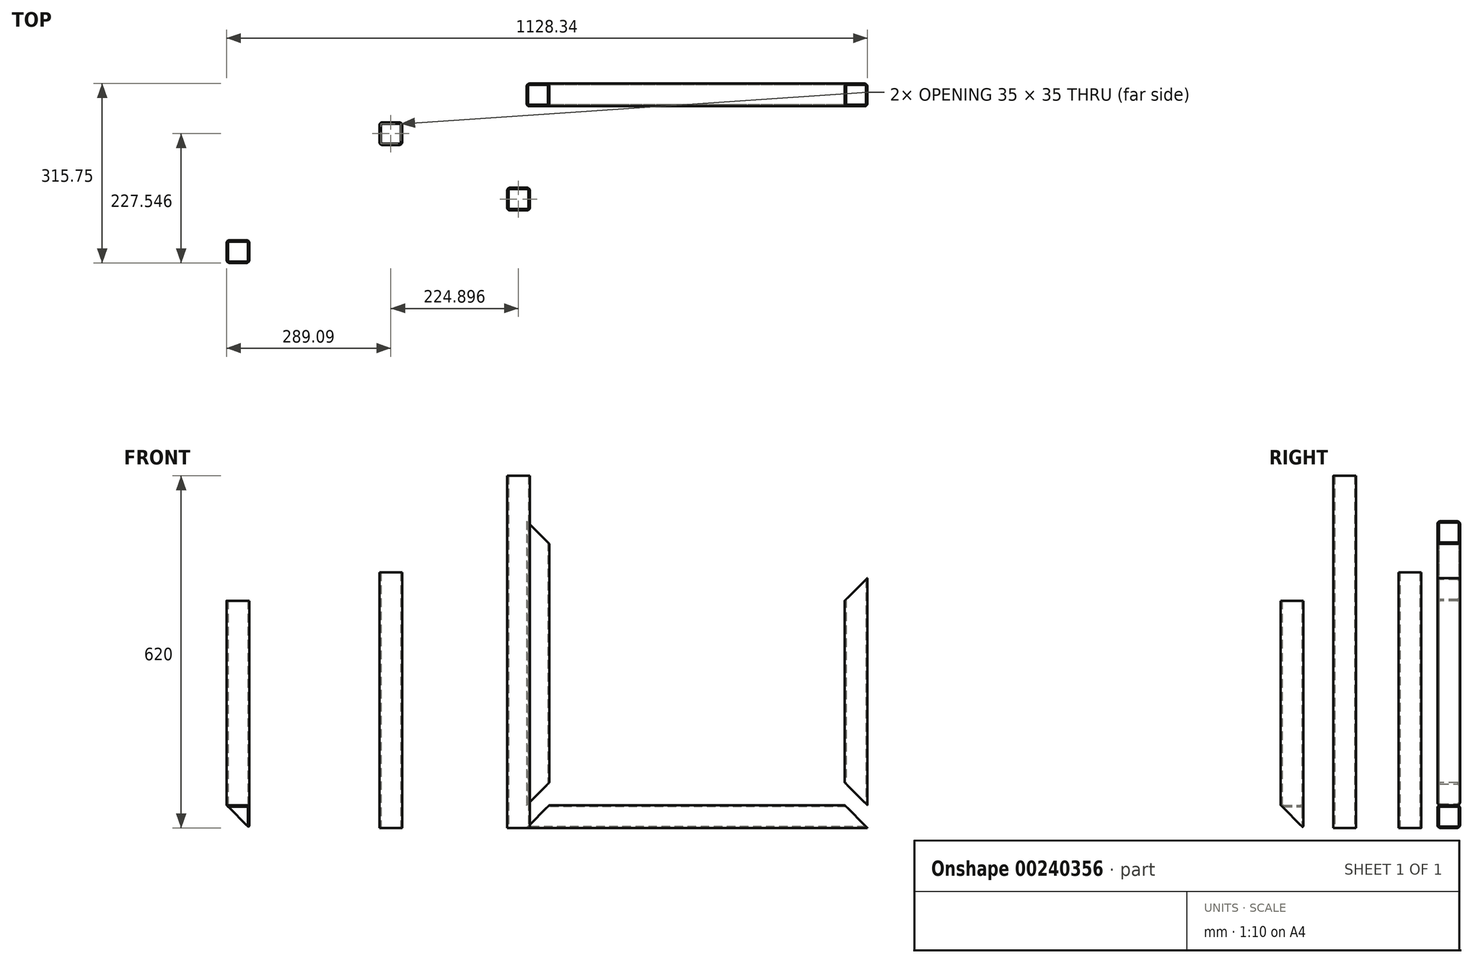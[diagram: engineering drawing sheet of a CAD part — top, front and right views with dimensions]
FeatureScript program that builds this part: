
annotation { "Feature Type Name" : "Feature", "Feature Type Description" : "" }
export const myFeature = defineFeature(function(context is Context, id is Id, definition is map)
    precondition{}
    {
        {
            var Q0;
            Q0=qCreatedBy(makeId("Right.planeOp"),FACE);
            var sketch = newSketch(context, id + "F0", { "sketchPlane" : qUnion([Q0])});
            skLineSegment(sketch, "E0.bottom", {"start": v(5, 0) * mm, "end": v(35, 0) * mm});
            skLineSegment(sketch, "E0.top", {"start": v(5, 40) * mm, "end": v(35, 40) * mm});
            skLineSegment(sketch, "E0.left", {"start": v(0, 5) * mm, "end": v(0, 35) * mm});
            skLineSegment(sketch, "E0.right", {"start": v(40, 5) * mm, "end": v(40, 35) * mm});
            skPoint(sketch, "E1.visualSharp", {"position": v(0, 40) * mm});
            skArc(sketch, "E1.filletArc", {"start": v(5, 40) * mm, "mid": v(1.46, 38.54) * mm, "end": v(0, 35) * mm});
            skPoint(sketch, "E2.visualSharp", {"position": v(40, 40) * mm});
            skArc(sketch, "E2.filletArc", {"start": v(40, 35) * mm, "mid": v(38.54, 38.54) * mm, "end": v(35, 40) * mm});
            skPoint(sketch, "E3.visualSharp", {"position": v(40, 0) * mm});
            skArc(sketch, "E3.filletArc", {"start": v(35, 0) * mm, "mid": v(38.54, 1.46) * mm, "end": v(40, 5) * mm});
            skPoint(sketch, "E4.visualSharp", {"position": v(0, 0) * mm});
            skArc(sketch, "E4.filletArc", {"start": v(0, 5) * mm, "mid": v(1.46, 1.46) * mm, "end": v(5, 0) * mm});
            skArc(sketch, "E5.0", {"start": v(35, 2.5) * mm, "mid": v(36.77, 3.23) * mm, "end": v(37.5, 5) * mm});
            skLineSegment(sketch, "E5.1", {"start": v(5, 2.5) * mm, "end": v(35, 2.5) * mm});
            skLineSegment(sketch, "E5.2", {"start": v(37.5, 5) * mm, "end": v(37.5, 35) * mm});
            skArc(sketch, "E5.3", {"start": v(2.5, 5) * mm, "mid": v(3.23, 3.23) * mm, "end": v(5, 2.5) * mm});
            skArc(sketch, "E5.4", {"start": v(37.5, 35) * mm, "mid": v(36.77, 36.77) * mm, "end": v(35, 37.5) * mm});
            skLineSegment(sketch, "E5.5", {"start": v(5, 37.5) * mm, "end": v(35, 37.5) * mm});
            skArc(sketch, "E5.6", {"start": v(5, 37.5) * mm, "mid": v(3.23, 36.77) * mm, "end": v(2.5, 35) * mm});
            skLineSegment(sketch, "E5.7", {"start": v(2.5, 5) * mm, "end": v(2.5, 35) * mm});
            skSolve(sketch);
        }
        {
            var Q0;
            Q0=makeQuery(id+"F0.imprint","IMPRINT",FACE,{"disambiguationData":[TD([[makeQuery(id+"F0.imprint","IMPRINT",EDGE,{"derivedFrom":sQuery(id+"F0.wireOp",EDGE,"E0.bottom")}),1.0]])]});
            extrude(context, id + "F1", {"entities" : qUnion([Q0]), "depth" : 600 * mm});
        }
        {
            var Q0;
            Q0=makeQuery(id+"F1.opExtrude","SWEPT_FACE",FACE,{"disambiguationData":[OSD([sQuery(id+"F0.wireOp",EDGE,"E0.left")])]});
            var sketch = newSketch(context, id + "F2", { "sketchPlane" : qUnion([Q0])});
            skLineSegment(sketch, "E6", {"start": v(0, 0) * mm, "end": v(0, 40) * mm});
            skLineSegment(sketch, "E7", {"start": v(0, 40) * mm, "end": v(40, 40) * mm});
            skLineSegment(sketch, "E8", {"start": v(40, 40) * mm, "end": v(0, 0) * mm});
            skLineSegment(sketch, "E9", {"start": v(600, 0) * mm, "end": v(600, 40) * mm});
            skLineSegment(sketch, "E10", {"start": v(600, 40) * mm, "end": v(560, 40) * mm});
            skLineSegment(sketch, "E11", {"start": v(560, 40) * mm, "end": v(600, 0) * mm});
            skSolve(sketch);
        }
        {
            var Q0;
            Q0 = qSketchRegion(id + "F2", true);
            extrude(context, id + "F3", {"entities" : qUnion([Q0]), "operationType" : NewBodyOperationType.REMOVE, "endBound" : BoundingType.THROUGH_ALL, "oppositeDirection" : true, "depth" : 25 * mm});
        }
        {
            var Q0;
            Q0=makeQuery(id+"F1.opExtrude","SWEPT_FACE",FACE,{"disambiguationData":[OSD([sQuery(id+"F0.wireOp",EDGE,"E0.top")])]});
            var sketch = newSketch(context, id + "F4", { "sketchPlane" : qUnion([Q0])});
            skLineSegment(sketch, "E12.bottom", {"start": v(5, 0) * mm, "end": v(35, 0) * mm});
            skLineSegment(sketch, "E12.top", {"start": v(5, 40) * mm, "end": v(35, 40) * mm});
            skLineSegment(sketch, "E12.left", {"start": v(0, 5) * mm, "end": v(0, 35) * mm});
            skLineSegment(sketch, "E12.right", {"start": v(40, 5) * mm, "end": v(40, 35) * mm});
            skPoint(sketch, "E13.visualSharp", {"position": v(0, 40) * mm});
            skArc(sketch, "E13.filletArc", {"start": v(5, 40) * mm, "mid": v(1.46, 38.54) * mm, "end": v(0, 35) * mm});
            skPoint(sketch, "E14.visualSharp", {"position": v(40, 40) * mm});
            skArc(sketch, "E14.filletArc", {"start": v(40, 35) * mm, "mid": v(38.54, 38.54) * mm, "end": v(35, 40) * mm});
            skPoint(sketch, "E15.visualSharp", {"position": v(40, 0) * mm});
            skArc(sketch, "E15.filletArc", {"start": v(35, 0) * mm, "mid": v(38.54, 1.46) * mm, "end": v(40, 5) * mm});
            skPoint(sketch, "E16.visualSharp", {"position": v(0, 0) * mm});
            skArc(sketch, "E16.filletArc", {"start": v(0, 5) * mm, "mid": v(1.46, 1.46) * mm, "end": v(5, 0) * mm});
            skArc(sketch, "E17.0", {"start": v(35, 2.5) * mm, "mid": v(36.77, 3.23) * mm, "end": v(37.5, 5) * mm});
            skLineSegment(sketch, "E17.1", {"start": v(5, 2.5) * mm, "end": v(35, 2.5) * mm});
            skLineSegment(sketch, "E17.2", {"start": v(37.5, 5) * mm, "end": v(37.5, 35) * mm});
            skArc(sketch, "E17.3", {"start": v(2.5, 5) * mm, "mid": v(3.23, 3.23) * mm, "end": v(5, 2.5) * mm});
            skArc(sketch, "E17.4", {"start": v(37.5, 35) * mm, "mid": v(36.77, 36.77) * mm, "end": v(35, 37.5) * mm});
            skLineSegment(sketch, "E17.5", {"start": v(5, 37.5) * mm, "end": v(35, 37.5) * mm});
            skArc(sketch, "E17.6", {"start": v(5, 37.5) * mm, "mid": v(3.23, 36.77) * mm, "end": v(2.5, 35) * mm});
            skLineSegment(sketch, "E17.7", {"start": v(2.5, 5) * mm, "end": v(2.5, 35) * mm});
            skSolve(sketch);
        }
        {
            var Q0;
            Q0=makeQuery(id+"F4.imprint","IMPRINT",FACE,{"disambiguationData":[TD([[makeQuery(id+"F4.imprint","IMPRINT",EDGE,{"derivedFrom":sQuery(id+"F4.wireOp",EDGE,"E12.bottom")}),1.0]])]});
            extrude(context, id + "F5", {"entities" : qUnion([Q0]), "depth" : 500 * mm});
        }
        {
            var Q0;
            Q0=makeQuery(id+"F5.opExtrude","SWEPT_FACE",FACE,{"disambiguationData":[OSD([sQuery(id+"F4.wireOp",EDGE,"E12.bottom")])]});
            var sketch = newSketch(context, id + "F6", { "sketchPlane" : qUnion([Q0])});
            skLineSegment(sketch, "E18", {"start": v(0, 40) * mm, "end": v(40, 40) * mm});
            skLineSegment(sketch, "E19", {"start": v(40, 40) * mm, "end": v(40, 80) * mm});
            skLineSegment(sketch, "E20", {"start": v(40, 80) * mm, "end": v(0, 40) * mm});
            skLineSegment(sketch, "E21", {"start": v(40, 540) * mm, "end": v(40, 500) * mm});
            skLineSegment(sketch, "E22", {"start": v(40, 500) * mm, "end": v(0, 540) * mm});
            skLineSegment(sketch, "E23", {"start": v(0, 540) * mm, "end": v(40, 540) * mm});
            skSolve(sketch);
        }
        {
            var Q0;
            Q0 = qSketchRegion(id + "F6", true);
            extrude(context, id + "F7", {"entities" : qUnion([Q0]), "operationType" : NewBodyOperationType.REMOVE, "endBound" : BoundingType.THROUGH_ALL, "oppositeDirection" : true, "depth" : 25 * mm});
        }
        {
            var Q0;
            Q0=makeQuery(id+"F1.opExtrude","SWEPT_FACE",FACE,{"disambiguationData":[OSD([sQuery(id+"F0.wireOp",EDGE,"E0.top")])]});
            var sketch = newSketch(context, id + "F8", { "sketchPlane" : qUnion([Q0])});
            skLineSegment(sketch, "E24.bottom", {"start": v(565, 0) * mm, "end": v(595, 0) * mm});
            skLineSegment(sketch, "E24.top", {"start": v(565, 40) * mm, "end": v(595, 40) * mm});
            skLineSegment(sketch, "E24.left", {"start": v(560, 5) * mm, "end": v(560, 35) * mm});
            skLineSegment(sketch, "E24.right", {"start": v(600, 5) * mm, "end": v(600, 35) * mm});
            skPoint(sketch, "E25.visualSharp", {"position": v(560, 40) * mm});
            skArc(sketch, "E25.filletArc", {"start": v(565, 40) * mm, "mid": v(561.46, 38.54) * mm, "end": v(560, 35) * mm});
            skPoint(sketch, "E26.visualSharp", {"position": v(600, 40) * mm});
            skArc(sketch, "E26.filletArc", {"start": v(600, 35) * mm, "mid": v(598.54, 38.54) * mm, "end": v(595, 40) * mm});
            skPoint(sketch, "E27.visualSharp", {"position": v(600, 0) * mm});
            skArc(sketch, "E27.filletArc", {"start": v(595, 0) * mm, "mid": v(598.54, 1.46) * mm, "end": v(600, 5) * mm});
            skPoint(sketch, "E28.visualSharp", {"position": v(560, 0) * mm});
            skArc(sketch, "E28.filletArc", {"start": v(560, 5) * mm, "mid": v(561.46, 1.46) * mm, "end": v(565, 0) * mm});
            skArc(sketch, "E29.0", {"start": v(595, 2.5) * mm, "mid": v(596.77, 3.23) * mm, "end": v(597.5, 5) * mm});
            skLineSegment(sketch, "E29.1", {"start": v(565, 2.5) * mm, "end": v(595, 2.5) * mm});
            skLineSegment(sketch, "E29.2", {"start": v(597.5, 5) * mm, "end": v(597.5, 35) * mm});
            skArc(sketch, "E29.3", {"start": v(562.5, 5) * mm, "mid": v(563.23, 3.23) * mm, "end": v(565, 2.5) * mm});
            skArc(sketch, "E29.4", {"start": v(597.5, 35) * mm, "mid": v(596.77, 36.77) * mm, "end": v(595, 37.5) * mm});
            skLineSegment(sketch, "E29.5", {"start": v(565, 37.5) * mm, "end": v(595, 37.5) * mm});
            skArc(sketch, "E29.6", {"start": v(565, 37.5) * mm, "mid": v(563.23, 36.77) * mm, "end": v(562.5, 35) * mm});
            skLineSegment(sketch, "E29.7", {"start": v(562.5, 5) * mm, "end": v(562.5, 35) * mm});
            skSolve(sketch);
        }
        {
            var Q0;
            Q0 = qSketchRegion(id + "F8", true);
            extrude(context, id + "F9", {"entities" : qUnion([Q0]), "depth" : 400 * mm});
        }
        {
            var Q0;
            Q0=makeQuery(id+"F9.opExtrude","SWEPT_FACE",FACE,{"disambiguationData":[OSD([sQuery(id+"F8.wireOp",EDGE,"E24.bottom")])]});
            var sketch = newSketch(context, id + "F10", { "sketchPlane" : qUnion([Q0])});
            skLineSegment(sketch, "E30", {"start": v(600, 440) * mm, "end": v(560, 440) * mm});
            skLineSegment(sketch, "E31", {"start": v(560, 440) * mm, "end": v(560, 400) * mm});
            skLineSegment(sketch, "E32", {"start": v(560, 400) * mm, "end": v(600, 440) * mm});
            skLineSegment(sketch, "E33", {"start": v(560, 80) * mm, "end": v(560, 40) * mm});
            skLineSegment(sketch, "E34", {"start": v(560, 40) * mm, "end": v(600, 40) * mm});
            skLineSegment(sketch, "E35", {"start": v(600, 40) * mm, "end": v(560, 80) * mm});
            skSolve(sketch);
        }
        {
            var Q0;
            Q0 = qSketchRegion(id + "F10", true);
            extrude(context, id + "F11", {"entities" : qUnion([Q0]), "operationType" : NewBodyOperationType.REMOVE, "endBound" : BoundingType.THROUGH_ALL, "oppositeDirection" : true, "depth" : 25 * mm});
        }
        {
            var Q0;
            Q0=qCreatedBy(makeId("Top.planeOp"),FACE);
            var sketch = newSketch(context, id + "F12", { "sketchPlane" : qUnion([Q0])});
            skLineSegment(sketch, "E36.bottom", {"start": v(-29.35, -183.38) * mm, "end": v(0.65, -183.38) * mm});
            skLineSegment(sketch, "E36.top", {"start": v(-29.35, -143.38) * mm, "end": v(0.65, -143.38) * mm});
            skLineSegment(sketch, "E36.left", {"start": v(-34.35, -178.38) * mm, "end": v(-34.35, -148.38) * mm});
            skLineSegment(sketch, "E36.right", {"start": v(5.65, -178.38) * mm, "end": v(5.65, -148.38) * mm});
            skPoint(sketch, "E37.visualSharp", {"position": v(-34.35, -143.38) * mm});
            skArc(sketch, "E37.filletArc", {"start": v(-29.35, -143.38) * mm, "mid": v(-32.89, -144.84) * mm, "end": v(-34.35, -148.38) * mm});
            skPoint(sketch, "E38.visualSharp", {"position": v(5.65, -143.38) * mm});
            skArc(sketch, "E38.filletArc", {"start": v(5.65, -148.38) * mm, "mid": v(4.18, -144.84) * mm, "end": v(0.65, -143.38) * mm});
            skPoint(sketch, "E39.visualSharp", {"position": v(5.65, -183.38) * mm});
            skArc(sketch, "E39.filletArc", {"start": v(0.65, -183.38) * mm, "mid": v(4.18, -181.91) * mm, "end": v(5.65, -178.38) * mm});
            skPoint(sketch, "E40.visualSharp", {"position": v(-34.35, -183.38) * mm});
            skArc(sketch, "E40.filletArc", {"start": v(-34.35, -178.38) * mm, "mid": v(-32.89, -181.91) * mm, "end": v(-29.35, -183.38) * mm});
            skArc(sketch, "E41.0", {"start": v(0.65, -180.88) * mm, "mid": v(2.41, -180.15) * mm, "end": v(3.15, -178.38) * mm});
            skLineSegment(sketch, "E41.1", {"start": v(-29.35, -180.88) * mm, "end": v(0.65, -180.88) * mm});
            skLineSegment(sketch, "E41.2", {"start": v(3.15, -178.38) * mm, "end": v(3.15, -148.38) * mm});
            skArc(sketch, "E41.3", {"start": v(-31.85, -178.38) * mm, "mid": v(-31.12, -180.15) * mm, "end": v(-29.35, -180.88) * mm});
            skArc(sketch, "E41.4", {"start": v(3.15, -148.38) * mm, "mid": v(2.41, -146.61) * mm, "end": v(0.65, -145.88) * mm});
            skLineSegment(sketch, "E41.5", {"start": v(-29.35, -145.88) * mm, "end": v(0.65, -145.88) * mm});
            skArc(sketch, "E41.6", {"start": v(-29.35, -145.88) * mm, "mid": v(-31.12, -146.61) * mm, "end": v(-31.85, -148.38) * mm});
            skLineSegment(sketch, "E41.7", {"start": v(-31.85, -178.38) * mm, "end": v(-31.85, -148.38) * mm});
            skSolve(sketch);
        }
        {
            var Q0;
            Q0=makeQuery(id+"F12.imprint","IMPRINT",FACE,{"disambiguationData":[TD([[makeQuery(id+"F12.imprint","IMPRINT",EDGE,{"derivedFrom":sQuery(id+"F12.wireOp",EDGE,"E36.bottom")}),1.0]])]});
            extrude(context, id + "F13", {"entities" : qUnion([Q0]), "depth" : 620 * mm});
        }
        {
            var Q0;
            Q0=qCreatedBy(makeId("Top.planeOp"),FACE);
            var sketch = newSketch(context, id + "F14", { "sketchPlane" : qUnion([Q0])});
            skLineSegment(sketch, "E42.bottom", {"start": v(-254.25, -68.2) * mm, "end": v(-224.25, -68.2) * mm});
            skLineSegment(sketch, "E42.top", {"start": v(-254.25, -28.2) * mm, "end": v(-224.25, -28.2) * mm});
            skLineSegment(sketch, "E42.left", {"start": v(-259.25, -63.2) * mm, "end": v(-259.25, -33.2) * mm});
            skLineSegment(sketch, "E42.right", {"start": v(-219.25, -63.2) * mm, "end": v(-219.25, -33.2) * mm});
            skPoint(sketch, "E43.visualSharp", {"position": v(-259.25, -28.2) * mm});
            skArc(sketch, "E43.filletArc", {"start": v(-254.25, -28.2) * mm, "mid": v(-257.79, -29.67) * mm, "end": v(-259.25, -33.2) * mm});
            skPoint(sketch, "E44.visualSharp", {"position": v(-219.25, -28.2) * mm});
            skArc(sketch, "E44.filletArc", {"start": v(-219.25, -33.2) * mm, "mid": v(-220.71, -29.67) * mm, "end": v(-224.25, -28.2) * mm});
            skPoint(sketch, "E45.visualSharp", {"position": v(-219.25, -68.2) * mm});
            skArc(sketch, "E45.filletArc", {"start": v(-224.25, -68.2) * mm, "mid": v(-220.71, -66.74) * mm, "end": v(-219.25, -63.2) * mm});
            skPoint(sketch, "E46.visualSharp", {"position": v(-259.25, -68.2) * mm});
            skArc(sketch, "E46.filletArc", {"start": v(-259.25, -63.2) * mm, "mid": v(-257.79, -66.74) * mm, "end": v(-254.25, -68.2) * mm});
            skArc(sketch, "E47.0", {"start": v(-224.25, -65.7) * mm, "mid": v(-222.48, -64.97) * mm, "end": v(-221.75, -63.2) * mm});
            skLineSegment(sketch, "E47.1", {"start": v(-254.25, -65.7) * mm, "end": v(-224.25, -65.7) * mm});
            skLineSegment(sketch, "E47.2", {"start": v(-221.75, -63.2) * mm, "end": v(-221.75, -33.2) * mm});
            skArc(sketch, "E47.3", {"start": v(-256.75, -63.2) * mm, "mid": v(-256.02, -64.97) * mm, "end": v(-254.25, -65.7) * mm});
            skArc(sketch, "E47.4", {"start": v(-221.75, -33.2) * mm, "mid": v(-222.48, -31.44) * mm, "end": v(-224.25, -30.7) * mm});
            skLineSegment(sketch, "E47.5", {"start": v(-254.25, -30.7) * mm, "end": v(-224.25, -30.7) * mm});
            skArc(sketch, "E47.6", {"start": v(-254.25, -30.7) * mm, "mid": v(-256.02, -31.44) * mm, "end": v(-256.75, -33.2) * mm});
            skLineSegment(sketch, "E47.7", {"start": v(-256.75, -63.2) * mm, "end": v(-256.75, -33.2) * mm});
            skSolve(sketch);
        }
        {
            var Q0;
            Q0=makeQuery(id+"F14.imprint","IMPRINT",FACE,{"disambiguationData":[TD([[makeQuery(id+"F14.imprint","IMPRINT",EDGE,{"derivedFrom":sQuery(id+"F14.wireOp",EDGE,"E42.bottom")}),1.0]])]});
            extrude(context, id + "F15", {"entities" : qUnion([Q0]), "depth" : 450 * mm});
        }
        {
            var Q0;
            Q0=qCreatedBy(makeId("Top.planeOp"),FACE);
            var sketch = newSketch(context, id + "F16", { "sketchPlane" : qUnion([Q0])});
            skLineSegment(sketch, "E48.bottom", {"start": v(-523.34, -275.75) * mm, "end": v(-493.34, -275.75) * mm});
            skLineSegment(sketch, "E48.top", {"start": v(-523.34, -235.75) * mm, "end": v(-493.34, -235.75) * mm});
            skLineSegment(sketch, "E48.left", {"start": v(-528.34, -270.75) * mm, "end": v(-528.34, -240.75) * mm});
            skLineSegment(sketch, "E48.right", {"start": v(-488.34, -270.75) * mm, "end": v(-488.34, -240.75) * mm});
            skPoint(sketch, "E49.visualSharp", {"position": v(-528.34, -235.75) * mm});
            skArc(sketch, "E49.filletArc", {"start": v(-523.34, -235.75) * mm, "mid": v(-526.87, -237.21) * mm, "end": v(-528.34, -240.75) * mm});
            skPoint(sketch, "E50.visualSharp", {"position": v(-488.34, -235.75) * mm});
            skArc(sketch, "E50.filletArc", {"start": v(-488.34, -240.75) * mm, "mid": v(-489.8, -237.21) * mm, "end": v(-493.34, -235.75) * mm});
            skPoint(sketch, "E51.visualSharp", {"position": v(-488.34, -275.75) * mm});
            skArc(sketch, "E51.filletArc", {"start": v(-493.34, -275.75) * mm, "mid": v(-489.8, -274.29) * mm, "end": v(-488.34, -270.75) * mm});
            skPoint(sketch, "E52.visualSharp", {"position": v(-528.34, -275.75) * mm});
            skArc(sketch, "E52.filletArc", {"start": v(-528.34, -270.75) * mm, "mid": v(-526.87, -274.29) * mm, "end": v(-523.34, -275.75) * mm});
            skArc(sketch, "E53.0", {"start": v(-493.34, -273.25) * mm, "mid": v(-491.57, -272.52) * mm, "end": v(-490.84, -270.75) * mm});
            skLineSegment(sketch, "E53.1", {"start": v(-523.34, -273.25) * mm, "end": v(-493.34, -273.25) * mm});
            skLineSegment(sketch, "E53.2", {"start": v(-490.84, -270.75) * mm, "end": v(-490.84, -240.75) * mm});
            skArc(sketch, "E53.3", {"start": v(-525.84, -270.75) * mm, "mid": v(-525.1, -272.52) * mm, "end": v(-523.34, -273.25) * mm});
            skArc(sketch, "E53.4", {"start": v(-490.84, -240.75) * mm, "mid": v(-491.57, -238.98) * mm, "end": v(-493.34, -238.25) * mm});
            skLineSegment(sketch, "E53.5", {"start": v(-523.34, -238.25) * mm, "end": v(-493.34, -238.25) * mm});
            skArc(sketch, "E53.6", {"start": v(-523.34, -238.25) * mm, "mid": v(-525.1, -238.98) * mm, "end": v(-525.84, -240.75) * mm});
            skLineSegment(sketch, "E53.7", {"start": v(-525.84, -270.75) * mm, "end": v(-525.84, -240.75) * mm});
            skSolve(sketch);
        }
        {
            var Q0;
            Q0=makeQuery(id+"F16.imprint","IMPRINT",FACE,{"disambiguationData":[TD([[makeQuery(id+"F16.imprint","IMPRINT",EDGE,{"derivedFrom":sQuery(id+"F16.wireOp",EDGE,"E48.bottom")}),1.0]])]});
            extrude(context, id + "F17", {"entities" : qUnion([Q0]), "depth" : 400 * mm});
        }
        {
            var Q0;
            Q0=makeQuery(id+"F17.opExtrude","SWEPT_FACE",FACE,{"disambiguationData":[OSD([sQuery(id+"F16.wireOp",EDGE,"E48.right")])]});
            var sketch = newSketch(context, id + "F18", { "sketchPlane" : qUnion([Q0])});
            skLineSegment(sketch, "E54", {"start": v(-235.75, 0) * mm, "end": v(-275.75, 40) * mm});
            skLineSegment(sketch, "E55", {"start": v(-235.75, 0) * mm, "end": v(-275.75, 0) * mm});
            skLineSegment(sketch, "E56", {"start": v(-275.75, 0) * mm, "end": v(-275.75, 40) * mm});
            skSolve(sketch);
        }
        {
            var Q0;
            Q0=makeQuery(id+"F17.opExtrude","SWEPT_FACE",FACE,{"disambiguationData":[OSD([sQuery(id+"F16.wireOp",EDGE,"E48.top")])]});
            var sketch = newSketch(context, id + "F19", { "sketchPlane" : qUnion([Q0])});
            skLineSegment(sketch, "E57.MirrorCS", {"start": v(528.34, 40) * mm, "end": v(488.34, 0) * mm});
            skLineSegment(sketch, "E58", {"start": v(488.34, 0) * mm, "end": v(528.34, 0) * mm});
            skLineSegment(sketch, "E59", {"start": v(528.34, 0) * mm, "end": v(528.34, 40) * mm});
            skSolve(sketch);
        }
        {
            var Q0;
            Q0 = qSketchRegion(id + "F18", true);
            extrude(context, id + "F20", {"entities" : qUnion([Q0]), "operationType" : NewBodyOperationType.REMOVE, "endBound" : BoundingType.THROUGH_ALL, "oppositeDirection" : true, "depth" : 25 * mm});
        }
        {
            var Q0;
            Q0 = qSketchRegion(id + "F19", true);
            extrude(context, id + "F21", {"entities" : qUnion([Q0]), "operationType" : NewBodyOperationType.REMOVE, "endBound" : BoundingType.THROUGH_ALL, "oppositeDirection" : true, "depth" : 25 * mm});
        }
    });
